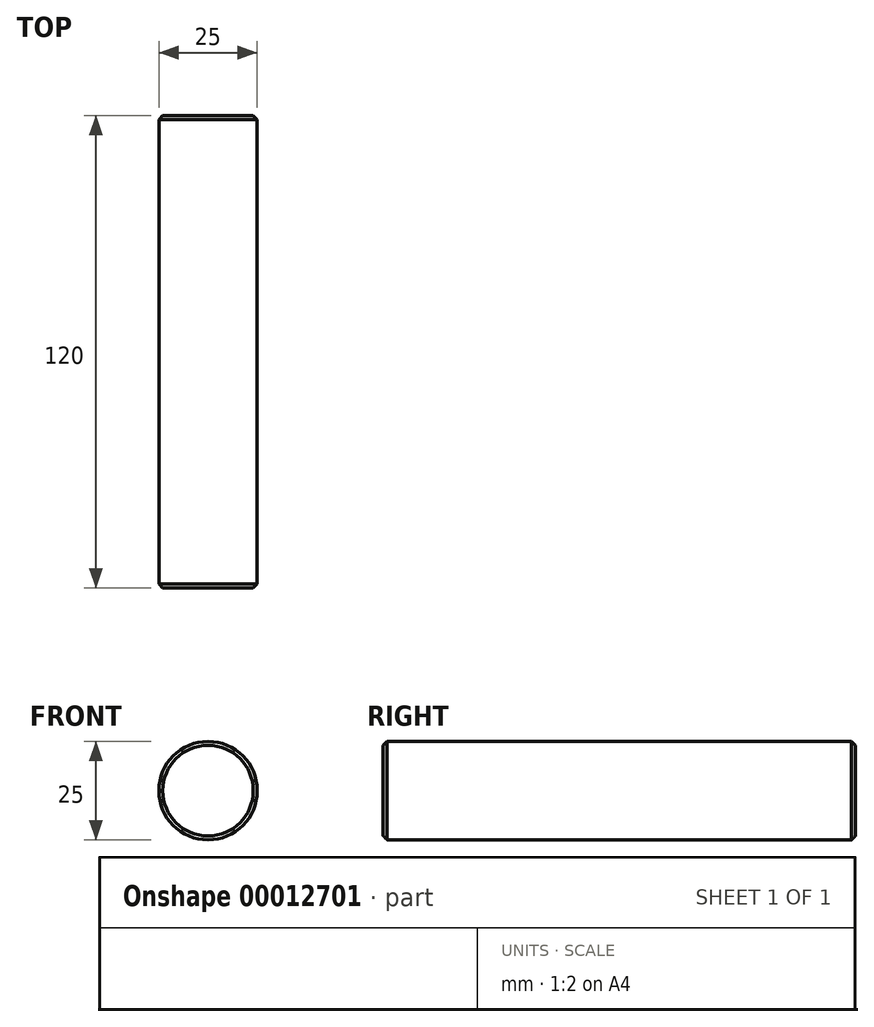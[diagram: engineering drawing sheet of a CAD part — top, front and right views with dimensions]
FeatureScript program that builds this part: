
annotation { "Feature Type Name" : "Feature", "Feature Type Description" : "" }
export const myFeature = defineFeature(function(context is Context, id is Id, definition is map)
    precondition{}
    {
        {
            var Q0;
            Q0=qCreatedBy(makeId("Front.planeOp"),FACE);
            var sketch = newSketch(context, id + "F0", { "sketchPlane" : qUnion([Q0])});
            skCircle(sketch, "E0", {"center": v(0, 0) * mm, "radius": 12.5 * mm});
            skSolve(sketch);
        }
        {
            var Q0;
            Q0 = qSketchRegion(id + "F0", true);
            var Q1;
            Q1=sQuery(id+"F0.wireOp",EDGE,"E0");
            extrude(context, id + "F1", {"entities" : qUnion([Q0]), "surfaceEntities" : qUnion([Q1]), "depth" : 120 * mm, "symmetric" : true});
        }
        {
            var Q0;
            Q0=makeQuery(id+"F1.opExtrude","CAP_EDGE",EDGE,{"disambiguationData":[OSD([sQuery(id+"F0.wireOp",EDGE,"E0")])],"isStart":false});
            var Q1;
            Q1=makeQuery(id+"F1.opExtrude","CAP_EDGE",EDGE,{"disambiguationData":[OSD([sQuery(id+"F0.wireOp",EDGE,"E0")])],"isStart":true});
            chamfer(context, id + "F2", {"entities" : qUnion([Q0, Q1]), "width" : 1 * mm, "tangentPropagation" : true});
        }
    });
